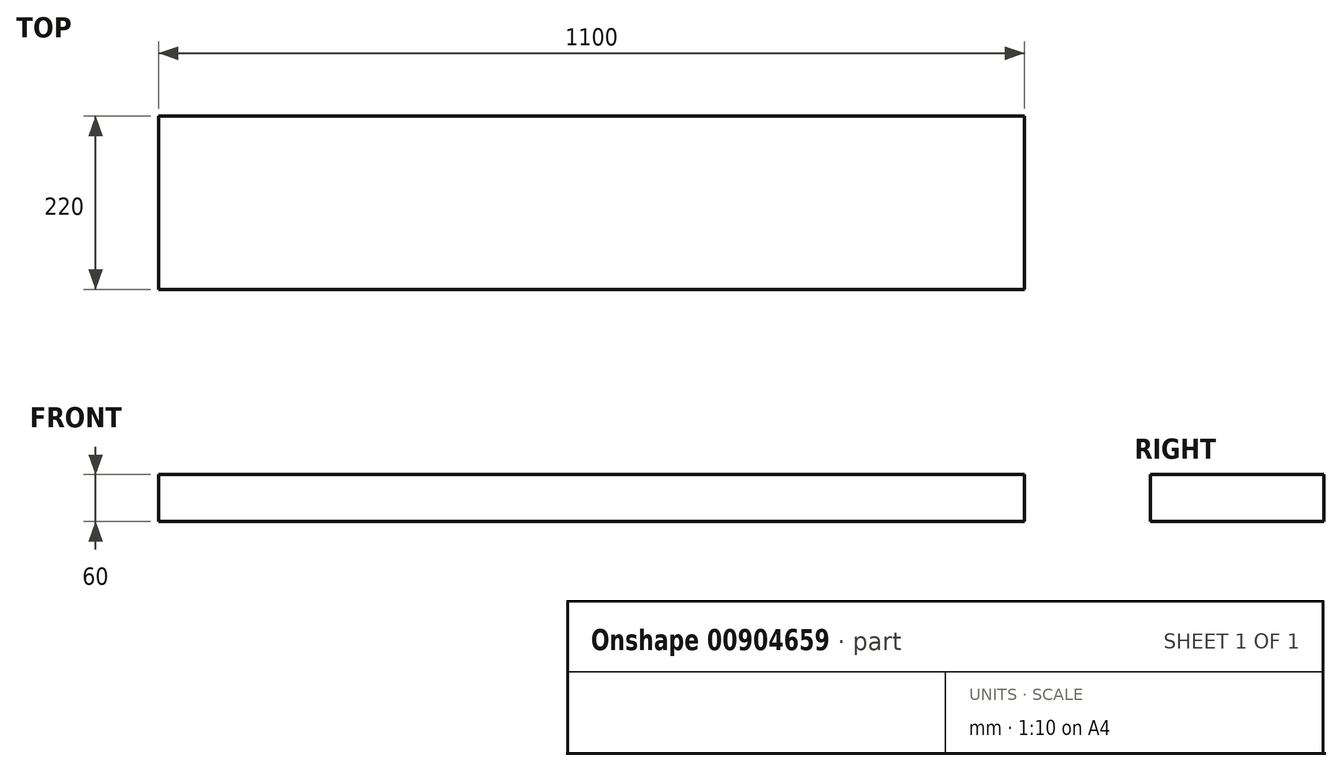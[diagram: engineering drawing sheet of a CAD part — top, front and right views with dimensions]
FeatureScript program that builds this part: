
annotation { "Feature Type Name" : "Feature", "Feature Type Description" : "" }
export const myFeature = defineFeature(function(context is Context, id is Id, definition is map)
    precondition{}
    {
        {
            var Q0;
            Q0=qCreatedBy(makeId("Top.planeOp"),FACE);
            var sketch = newSketch(context, id + "F0", { "sketchPlane" : qUnion([Q0])});
            skLineSegment(sketch, "E0.bottom", {"start": v(0, 0) * mm, "end": v(-1100, 0) * mm});
            skLineSegment(sketch, "E0.top", {"start": v(0, 220) * mm, "end": v(-1100, 220) * mm});
            skLineSegment(sketch, "E0.left", {"start": v(0, 0) * mm, "end": v(0, 220) * mm});
            skLineSegment(sketch, "E0.right", {"start": v(-1100, 0) * mm, "end": v(-1100, 220) * mm});
            skSolve(sketch);
        }
        {
            var Q0;
            Q0 = qSketchRegion(id + "F0", true);
            extrude(context, id + "F1", {"entities" : qUnion([Q0]), "depth" : 60 * mm, "offsetDistance" : 25 * mm});
        }
    });
